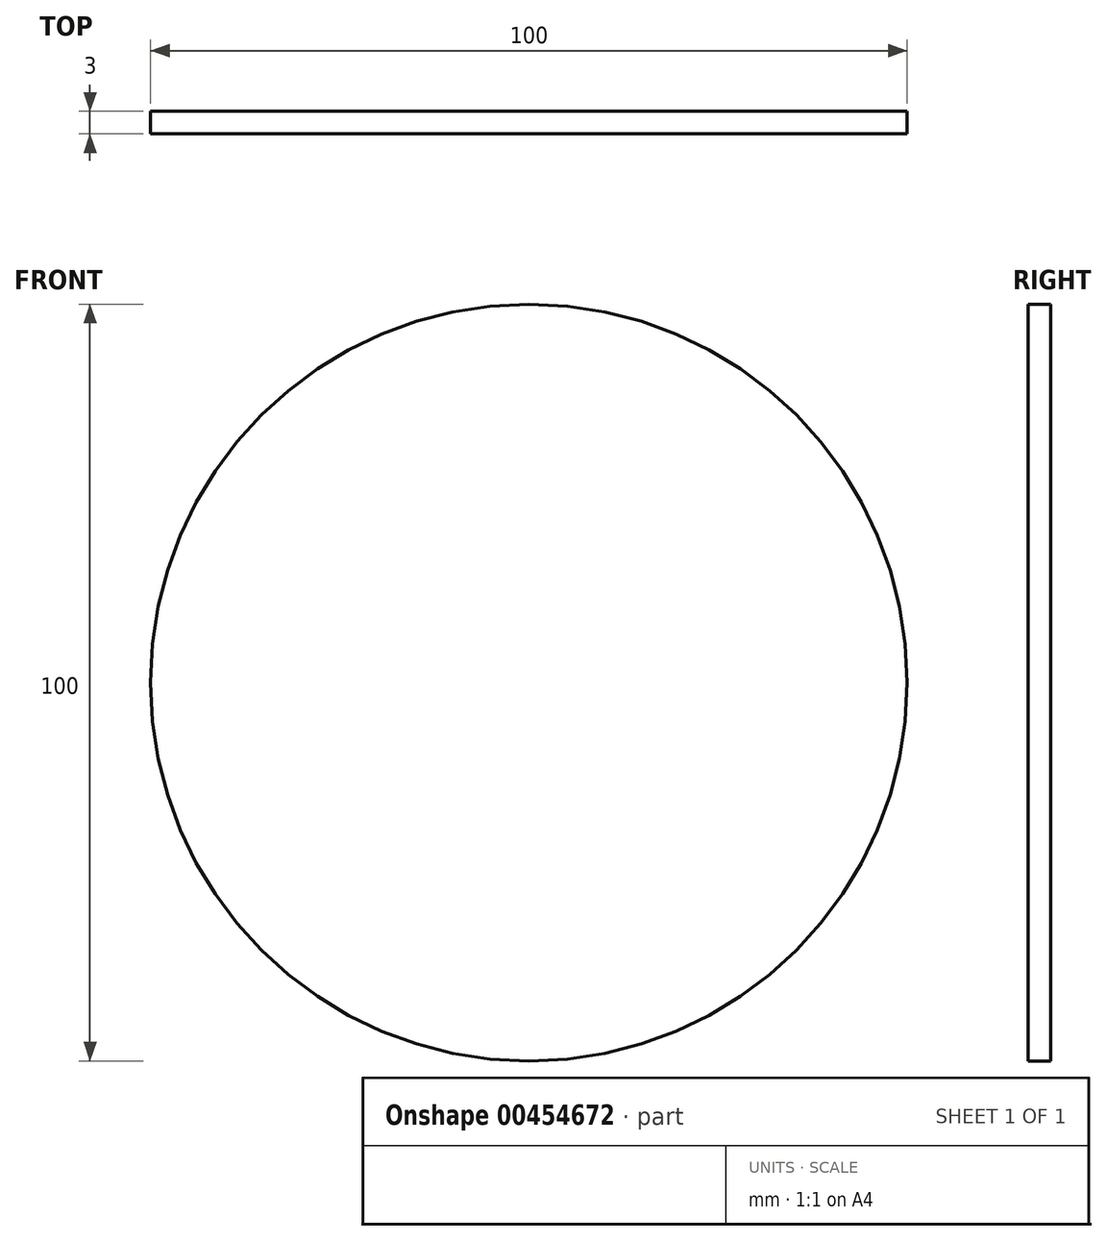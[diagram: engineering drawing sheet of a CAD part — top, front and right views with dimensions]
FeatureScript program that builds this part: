
annotation { "Feature Type Name" : "Feature", "Feature Type Description" : "" }
export const myFeature = defineFeature(function(context is Context, id is Id, definition is map)
    precondition{}
    {
        {
            var Q0;
            Q0=qCreatedBy(makeId("Front.planeOp"),FACE);
            var sketch = newSketch(context, id + "F0", { "sketchPlane" : qUnion([Q0])});
            skCircle(sketch, "E0", {"center": v(0, 0) * mm, "radius": 50 * mm});
            skLineSegment(sketch, "E1", {"start": v(0, 0) * mm, "end": v(0, 150) * mm});
            skLineSegment(sketch, "E2", {"start": v(0, 0) * mm, "end": v(0, -150) * mm});
            skLineSegment(sketch, "E3", {"start": v(0, 0) * mm, "end": v(150, 0) * mm});
            skLineSegment(sketch, "E4", {"start": v(0, 0) * mm, "end": v(-150, 0) * mm});
            skSolve(sketch);
        }
        {
            var Q0;
            Q0 = qSketchRegion(id + "F0", true);
            extrude(context, id + "F1", {"entities" : qUnion([Q0]), "depth" : 3 * mm});
        }
    });
